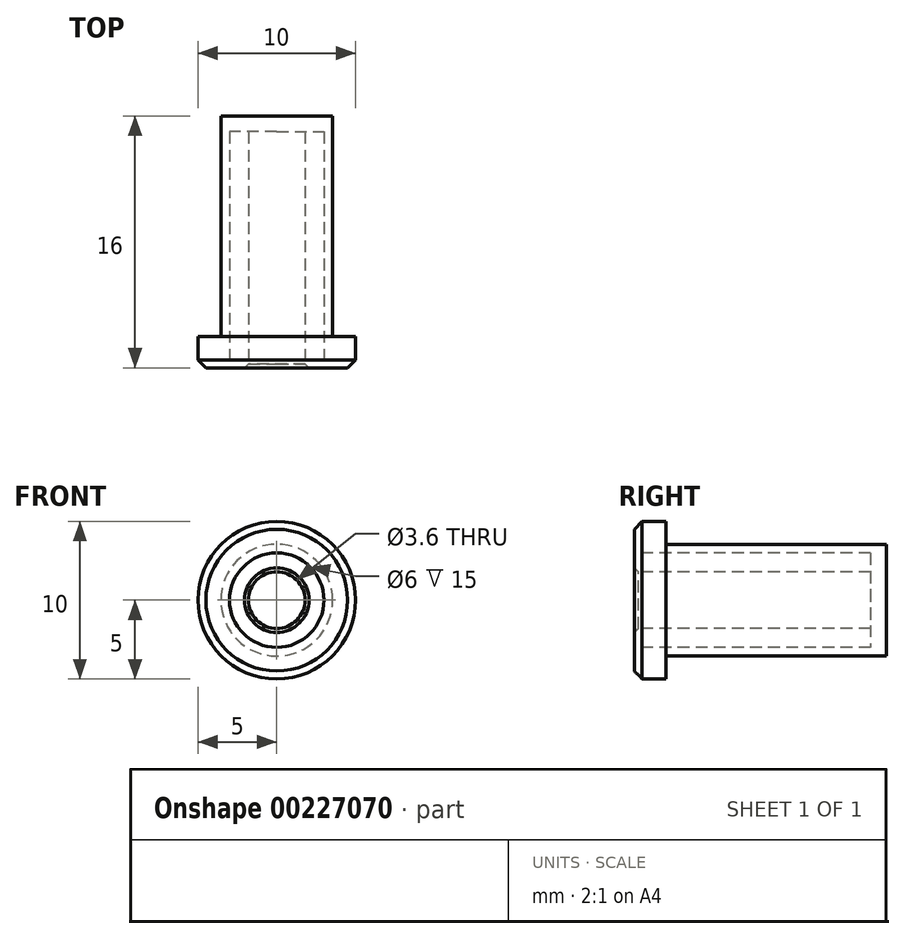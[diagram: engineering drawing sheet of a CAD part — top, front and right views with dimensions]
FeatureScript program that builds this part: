
annotation { "Feature Type Name" : "Feature", "Feature Type Description" : "" }
export const myFeature = defineFeature(function(context is Context, id is Id, definition is map)
    precondition{}
    {
        {
            var Q0;
            Q0=qCreatedBy(makeId("Front.planeOp"),FACE);
            var sketch = newSketch(context, id + "F0", { "sketchPlane" : qUnion([Q0])});
            skCircle(sketch, "E0", {"center": v(0, 0) * mm, "radius": 5 * mm});
            skSolve(sketch);
        }
        {
            var Q0;
            Q0=makeQuery(id+"F0.imprint","IMPRINT",FACE,{"disambiguationData":[TD([[makeQuery(id+"F0.imprint","IMPRINT",EDGE,{"derivedFrom":sQuery(id+"F0.wireOp",EDGE,"E0")}),1.0]])]});
            extrude(context, id + "F1", {"entities" : qUnion([Q0]), "depth" : 2 * mm, "offsetDistance" : 25 * mm});
        }
        {
            var Q0;
            Q0=makeQuery(id+"F1.opExtrude","CAP_FACE",FACE,{"disambiguationData":[OSD([sQuery(id+"F0.wireOp",EDGE,"E0")])],"isStart":true});
            var sketch = newSketch(context, id + "F2", { "sketchPlane" : qUnion([Q0])});
            skCircle(sketch, "E1", {"center": v(0, 0) * mm, "radius": 3.55 * mm});
            skSolve(sketch);
        }
        {
            var Q0;
            Q0=makeQuery(id+"F2.imprint","IMPRINT",FACE,{"disambiguationData":[TD([[makeQuery(id+"F2.imprint","IMPRINT",EDGE,{"derivedFrom":sQuery(id+"F2.wireOp",EDGE,"E1")}),1.0]])]});
            extrude(context, id + "F3", {"entities" : qUnion([Q0]), "operationType" : NewBodyOperationType.ADD, "depth" : 14 * mm, "offsetDistance" : 25 * mm});
        }
        {
            var Q0;
            Q0=makeQuery(id+"F1.opExtrude","CAP_FACE",FACE,{"disambiguationData":[OSD([sQuery(id+"F0.wireOp",EDGE,"E0")])],"isStart":false});
            var sketch = newSketch(context, id + "F4", { "sketchPlane" : qUnion([Q0])});
            skCircle(sketch, "E2", {"center": v(0, 0) * mm, "radius": 3 * mm});
            skSolve(sketch);
        }
        {
            var Q0;
            Q0=makeQuery(id+"F4.imprint","IMPRINT",FACE,{"disambiguationData":[TD([[makeQuery(id+"F4.imprint","IMPRINT",EDGE,{"derivedFrom":sQuery(id+"F4.wireOp",EDGE,"E2")}),1.0]])]});
            var Q1;
            Q1=makeQuery(id+"F3.opExtrude","CAP_FACE",FACE,{"disambiguationData":[OSD([sQuery(id+"F2.wireOp",EDGE,"E1")])],"isStart":false});
            extrude(context, id + "F5", {"entities" : qUnion([Q0]), "operationType" : NewBodyOperationType.REMOVE, "endBound" : BoundingType.UP_TO_SURFACE, "oppositeDirection" : true, "depth" : 25 * mm, "endBoundEntityFace" : qUnion([Q1]), "hasOffset" : true, "offsetDistance" : 1 * mm});
        }
        {
            var Q0;
            Q0=makeQuery(id+"F1.opExtrude","CAP_FACE",FACE,{"disambiguationData":[OSD([sQuery(id+"F0.wireOp",EDGE,"E0")])],"isStart":false});
            var sketch = newSketch(context, id + "F6", { "sketchPlane" : qUnion([Q0])});
            skCircle(sketch, "E3.0", {"center": v(0, 0) * mm, "radius": 1.8 * mm});
            skSolve(sketch);
        }
        {
            var Q0;
            Q0=makeQuery(id+"F6.imprint","IMPRINT",FACE,{"disambiguationData":[TD([[makeQuery(id+"F6.imprint","IMPRINT",EDGE,{"derivedFrom":sQuery(id+"F6.wireOp",EDGE,"E3.0")}),-1.0]])]});
            var Q1;
            Q1=makeQuery(id+"F5.boolean.opBoolean","COPY",FACE,{"derivedFrom":makeQuery(id+"F5.opExtrude","CAP_FACE",FACE,{"disambiguationData":[OSD([sQuery(id+"F4.wireOp",EDGE,"E2")])],"isStart":false})});
            extrude(context, id + "F7", {"entities" : qUnion([Q0]), "endBound" : BoundingType.UP_TO_SURFACE, "oppositeDirection" : true, "depth" : 25 * mm, "endBoundEntityFace" : qUnion([Q1]), "offsetDistance" : 25 * mm});
        }
        {
            var Q0;
            Q0=makeQuery(id+"F7.opExtrude","CAP_EDGE",EDGE,{"disambiguationData":[OSD([sQuery(id+"F6.wireOp",EDGE,"E3.0")])],"isStart":true});
            chamfer(context, id + "F8", {"entities" : qUnion([Q0]), "width" : .25 * mm, "tangentPropagation" : true});
        }
        {
            var Q0;
            Q0=makeQuery(id+"F1.opExtrude","CAP_EDGE",EDGE,{"disambiguationData":[OSD([sQuery(id+"F0.wireOp",EDGE,"E0")])],"isStart":false});
            chamfer(context, id + "F9", {"entities" : qUnion([Q0]), "width" : .5 * mm, "tangentPropagation" : true});
        }
    });
